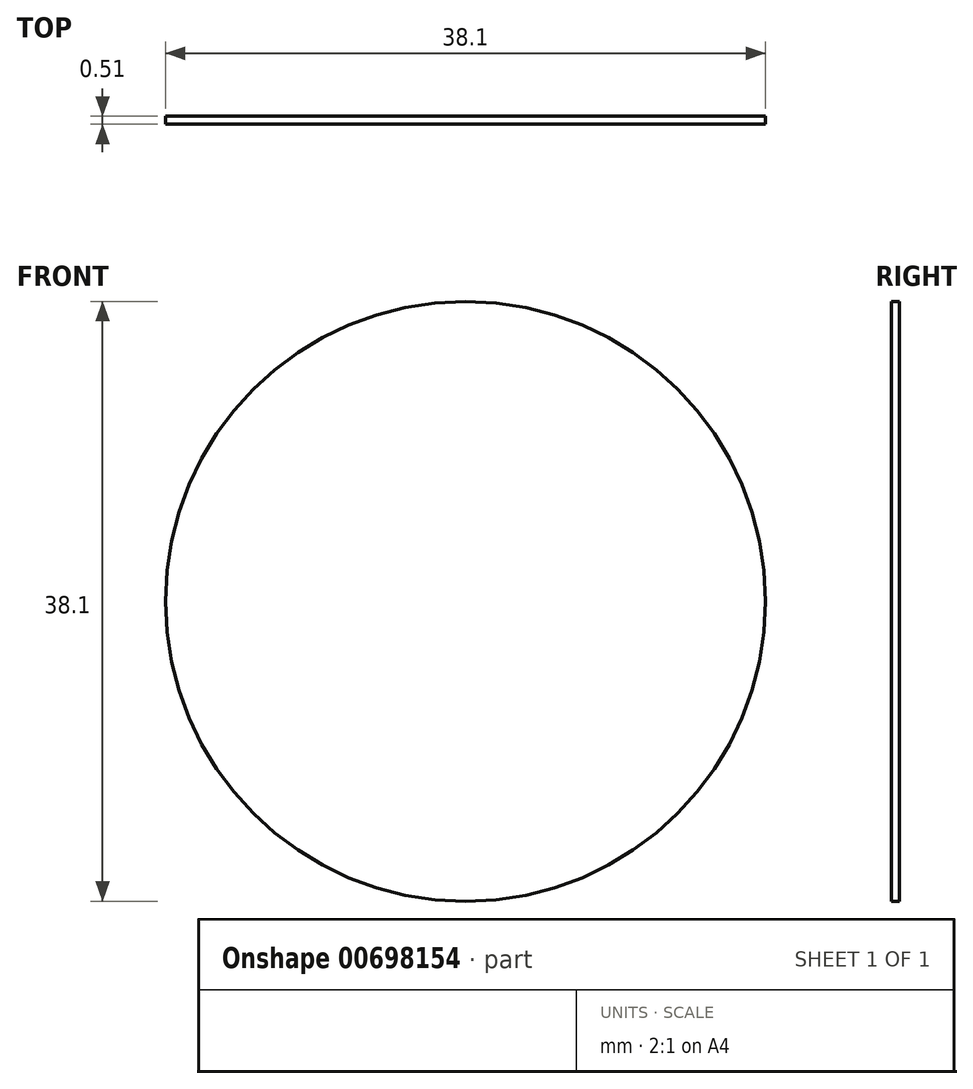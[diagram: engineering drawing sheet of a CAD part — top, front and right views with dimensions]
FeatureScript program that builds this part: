
annotation { "Feature Type Name" : "Feature", "Feature Type Description" : "" }
export const myFeature = defineFeature(function(context is Context, id is Id, definition is map)
    precondition{}
    {
        {
            var Q0;
            Q0=qCreatedBy(makeId("Front.planeOp"),FACE);
            var sketch = newSketch(context, id + "F0", { "sketchPlane" : qUnion([Q0])});
            skCircle(sketch, "E0", {"center": v(0, 0) * mm, "radius": 19.05 * mm});
            skSolve(sketch);
        }
        {
            var Q0;
            Q0=qSketchRegion(id+"F0",true);
            extrude(context, id + "F1", {"entities" : qUnion([Q0]), "depth" : 0.5 * mm, "offsetDistance" : 25.4 * mm});
        }
    });
